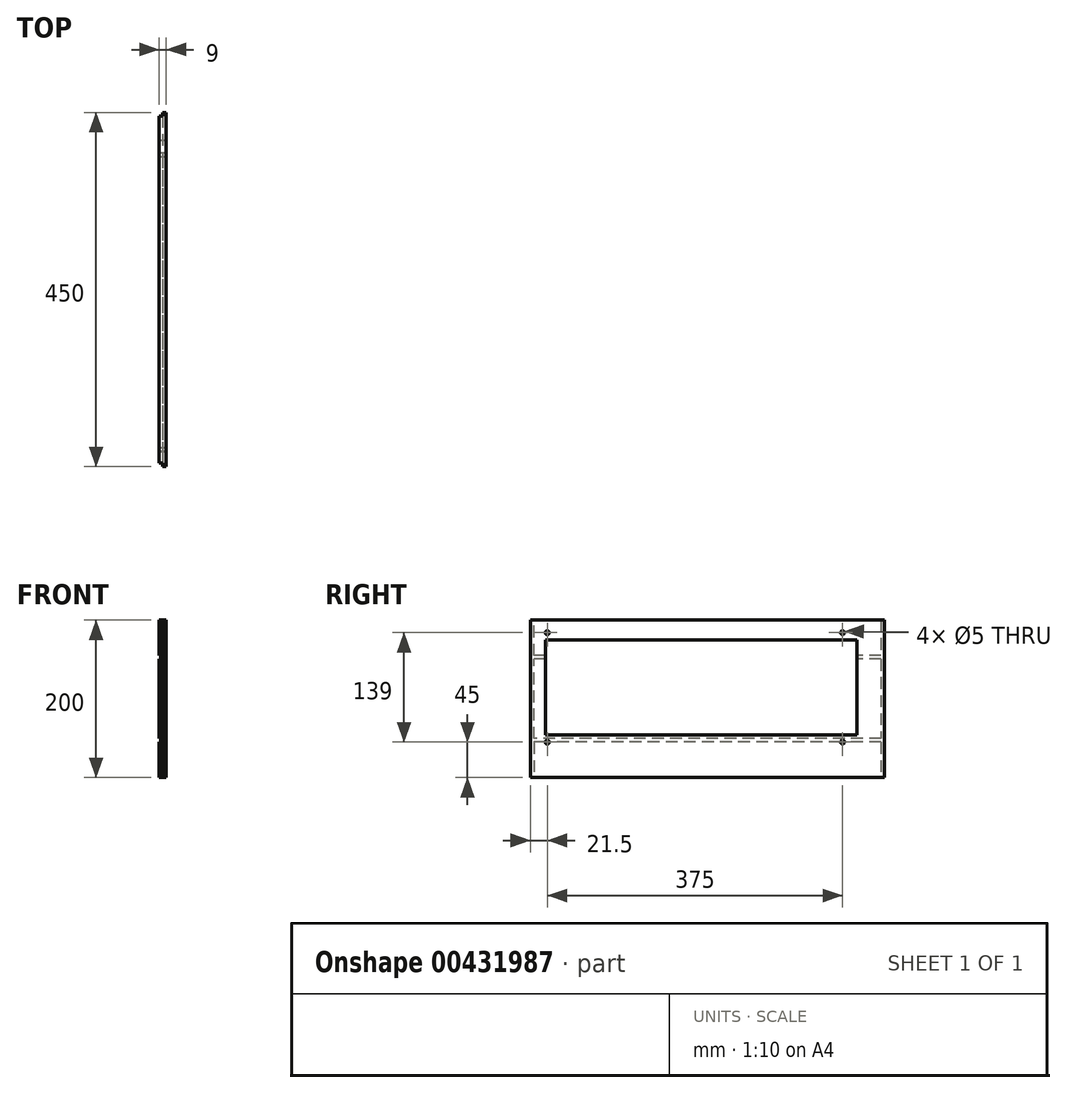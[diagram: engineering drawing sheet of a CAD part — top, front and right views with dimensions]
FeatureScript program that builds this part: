
annotation { "Feature Type Name" : "Feature", "Feature Type Description" : "" }
export const myFeature = defineFeature(function(context is Context, id is Id, definition is map)
    precondition{}
    {
        {
            var Q0;
            Q0=qCreatedBy(makeId("Right.planeOp"),FACE);
            var sketch = newSketch(context, id + "F0", { "sketchPlane" : qUnion([Q0])});
            skLineSegment(sketch, "E0.bottom", {"start": v(-225, 100) * mm, "end": v(225, 100) * mm});
            skLineSegment(sketch, "E0.top", {"start": v(-225, -100) * mm, "end": v(225, -100) * mm});
            skLineSegment(sketch, "E0.left", {"start": v(-225, 100) * mm, "end": v(-225, -100) * mm});
            skLineSegment(sketch, "E0.right", {"start": v(225, 100) * mm, "end": v(225, -100) * mm});
            skPoint(sketch, "E0.middle", {"position": v(0, 0) * mm});
            skSolve(sketch);
        }
        {
            var Q0;
            Q0=makeQuery(id+"F0.imprint","IMPRINT",FACE,{"disambiguationData":[TD([[makeQuery(id+"F0.imprint","IMPRINT",EDGE,{"derivedFrom":sQuery(id+"F0.wireOp",EDGE,"E0.bottom")}),-1.0]])]});
            extrude(context, id + "F1", {"entities" : qUnion([Q0]), "depth" : 9 * mm, "offsetDistance" : 25 * mm});
        }
        {
            var Q0;
            Q0=makeQuery(id+"F1.opExtrude","SWEPT_FACE",FACE,{"disambiguationData":[OSD([sQuery(id+"F0.wireOp",EDGE,"E0.left")])]});
            var sketch = newSketch(context, id + "F2", { "sketchPlane" : qUnion([Q0])});
            skLineSegment(sketch, "E1.bottom", {"start": v(0, -100) * mm, "end": v(4.5, -100) * mm});
            skLineSegment(sketch, "E1.top", {"start": v(0, 100) * mm, "end": v(4.5, 100) * mm});
            skLineSegment(sketch, "E1.left", {"start": v(0, -100) * mm, "end": v(0, 100) * mm});
            skLineSegment(sketch, "E1.right", {"start": v(4.5, -100) * mm, "end": v(4.5, 100) * mm});
            skSolve(sketch);
        }
        {
            var Q0;
            Q0=qSketchRegion(id+"F2",true);
            extrude(context, id + "F3", {"entities" : qUnion([Q0]), "operationType" : NewBodyOperationType.REMOVE, "oppositeDirection" : true, "depth" : 4.5 * mm, "offsetDistance" : 25 * mm});
        }
        {
            var Q0;
            Q0=makeQuery(id+"F1.opExtrude","SWEPT_FACE",FACE,{"disambiguationData":[OSD([sQuery(id+"F0.wireOp",EDGE,"E0.right")])]});
            var sketch = newSketch(context, id + "F4", { "sketchPlane" : qUnion([Q0])});
            skLineSegment(sketch, "E2.bottom", {"start": v(0, 100) * mm, "end": v(-4.5, 100) * mm});
            skLineSegment(sketch, "E2.top", {"start": v(0, -100) * mm, "end": v(-4.5, -100) * mm});
            skLineSegment(sketch, "E2.left", {"start": v(0, 100) * mm, "end": v(0, -100) * mm});
            skLineSegment(sketch, "E2.right", {"start": v(-4.5, 100) * mm, "end": v(-4.5, -100) * mm});
            skSolve(sketch);
        }
        {
            var Q0;
            Q0=qSketchRegion(id+"F4",true);
            extrude(context, id + "F5", {"entities" : qUnion([Q0]), "operationType" : NewBodyOperationType.REMOVE, "oppositeDirection" : true, "depth" : 4.5 * mm, "offsetDistance" : 25 * mm});
        }
        {
            var Q0;
            Q0=makeQuery(id+"F1.opExtrude","CAP_FACE",FACE,{"disambiguationData":[OSD([sQuery(id+"F0.wireOp",EDGE,"E0.bottom"),sQuery(id+"F0.wireOp",EDGE,"E0.top"),sQuery(id+"F0.wireOp",EDGE,"E0.left"),sQuery(id+"F0.wireOp",EDGE,"E0.right")])],"isStart":true});
            var sketch = newSketch(context, id + "F6", { "sketchPlane" : qUnion([Q0])});
            skLineSegment(sketch, "E3.bottom", {"start": v(-220.5, 55) * mm, "end": v(220.5, 55) * mm});
            skLineSegment(sketch, "E3.top", {"start": v(-220.5, 50.5) * mm, "end": v(220.5, 50.5) * mm});
            skLineSegment(sketch, "E3.left", {"start": v(-220.5, 55) * mm, "end": v(-220.5, 50.5) * mm});
            skLineSegment(sketch, "E3.right", {"start": v(220.5, 55) * mm, "end": v(220.5, 50.5) * mm});
            skSolve(sketch);
        }
        {
            var Q0;
            Q0 = qSketchRegion(id + "F6", true);
            extrude(context, id + "F7", {"entities" : qUnion([Q0]), "operationType" : NewBodyOperationType.REMOVE, "oppositeDirection" : true, "depth" : 4.5 * mm, "offsetDistance" : 25 * mm});
        }
        {
            var Q0;
            Q0=makeQuery(id+"F1.opExtrude","CAP_FACE",FACE,{"disambiguationData":[OSD([sQuery(id+"F0.wireOp",EDGE,"E0.bottom"),sQuery(id+"F0.wireOp",EDGE,"E0.top"),sQuery(id+"F0.wireOp",EDGE,"E0.left"),sQuery(id+"F0.wireOp",EDGE,"E0.right")])],"isStart":true});
            var sketch = newSketch(context, id + "F8", { "sketchPlane" : qUnion([Q0])});
            skLineSegment(sketch, "E4.bottom", {"start": v(-220.5, -55) * mm, "end": v(220.5, -55) * mm});
            skLineSegment(sketch, "E4.top", {"start": v(-220.5, -50.5) * mm, "end": v(220.5, -50.5) * mm});
            skLineSegment(sketch, "E4.left", {"start": v(-220.5, -55) * mm, "end": v(-220.5, -50.5) * mm});
            skLineSegment(sketch, "E4.right", {"start": v(220.5, -55) * mm, "end": v(220.5, -50.5) * mm});
            skSolve(sketch);
        }
        {
            var Q0;
            Q0=qSketchRegion(id+"F8",true);
            extrude(context, id + "F9", {"entities" : qUnion([Q0]), "operationType" : NewBodyOperationType.REMOVE, "oppositeDirection" : true, "depth" : 4.5 * mm, "offsetDistance" : 25 * mm});
        }
        {
            var Q0;
            Q0=makeQuery(id+"F1.opExtrude","CAP_FACE",FACE,{"disambiguationData":[OSD([sQuery(id+"F0.wireOp",EDGE,"E0.bottom"),sQuery(id+"F0.wireOp",EDGE,"E0.top"),sQuery(id+"F0.wireOp",EDGE,"E0.left"),sQuery(id+"F0.wireOp",EDGE,"E0.right")])],"isStart":false});
            var sketch = newSketch(context, id + "F10", { "sketchPlane" : qUnion([Q0])});
            skLineSegment(sketch, "E5.bottom", {"start": v(-205.5, 75) * mm, "end": v(189.5, 75) * mm});
            skLineSegment(sketch, "E5.top", {"start": v(-205.5, -46) * mm, "end": v(189.5, -46) * mm});
            skLineSegment(sketch, "E5.left", {"start": v(-205.5, 75) * mm, "end": v(-205.5, -46) * mm});
            skLineSegment(sketch, "E5.right", {"start": v(189.5, 75) * mm, "end": v(189.5, -46) * mm});
            skSolve(sketch);
        }
        {
            var Q0;
            Q0=qSketchRegion(id+"F10",true);
            extrude(context, id + "F11", {"entities" : qUnion([Q0]), "operationType" : NewBodyOperationType.REMOVE, "endBound" : BoundingType.UP_TO_NEXT, "oppositeDirection" : true, "depth" : 25 * mm});
        }
        {
            var Q0;
            Q0=makeQuery(id+"F1.opExtrude","CAP_FACE",FACE,{"disambiguationData":[OSD([sQuery(id+"F0.wireOp",EDGE,"E0.bottom"),sQuery(id+"F0.wireOp",EDGE,"E0.top"),sQuery(id+"F0.wireOp",EDGE,"E0.left"),sQuery(id+"F0.wireOp",EDGE,"E0.right")])],"isStart":false});
            var sketch = newSketch(context, id + "F12", { "sketchPlane" : qUnion([Q0])});
            skCircle(sketch, "E6", {"center": v(-203.5, 84) * mm, "radius": 2.5 * mm});
            skCircle(sketch, "E7", {"center": v(171.5, 84) * mm, "radius": 2.5 * mm});
            skCircle(sketch, "E8", {"center": v(171.5, -55) * mm, "radius": 2.5 * mm});
            skCircle(sketch, "E9", {"center": v(-203.5, -55) * mm, "radius": 2.5 * mm});
            skSolve(sketch);
        }
        {
            var Q0;
            Q0 = qSketchRegion(id + "F12", true);
            extrude(context, id + "F13", {"entities" : qUnion([Q0]), "operationType" : NewBodyOperationType.REMOVE, "endBound" : BoundingType.UP_TO_NEXT, "oppositeDirection" : true, "depth" : 25 * mm});
        }
    });
